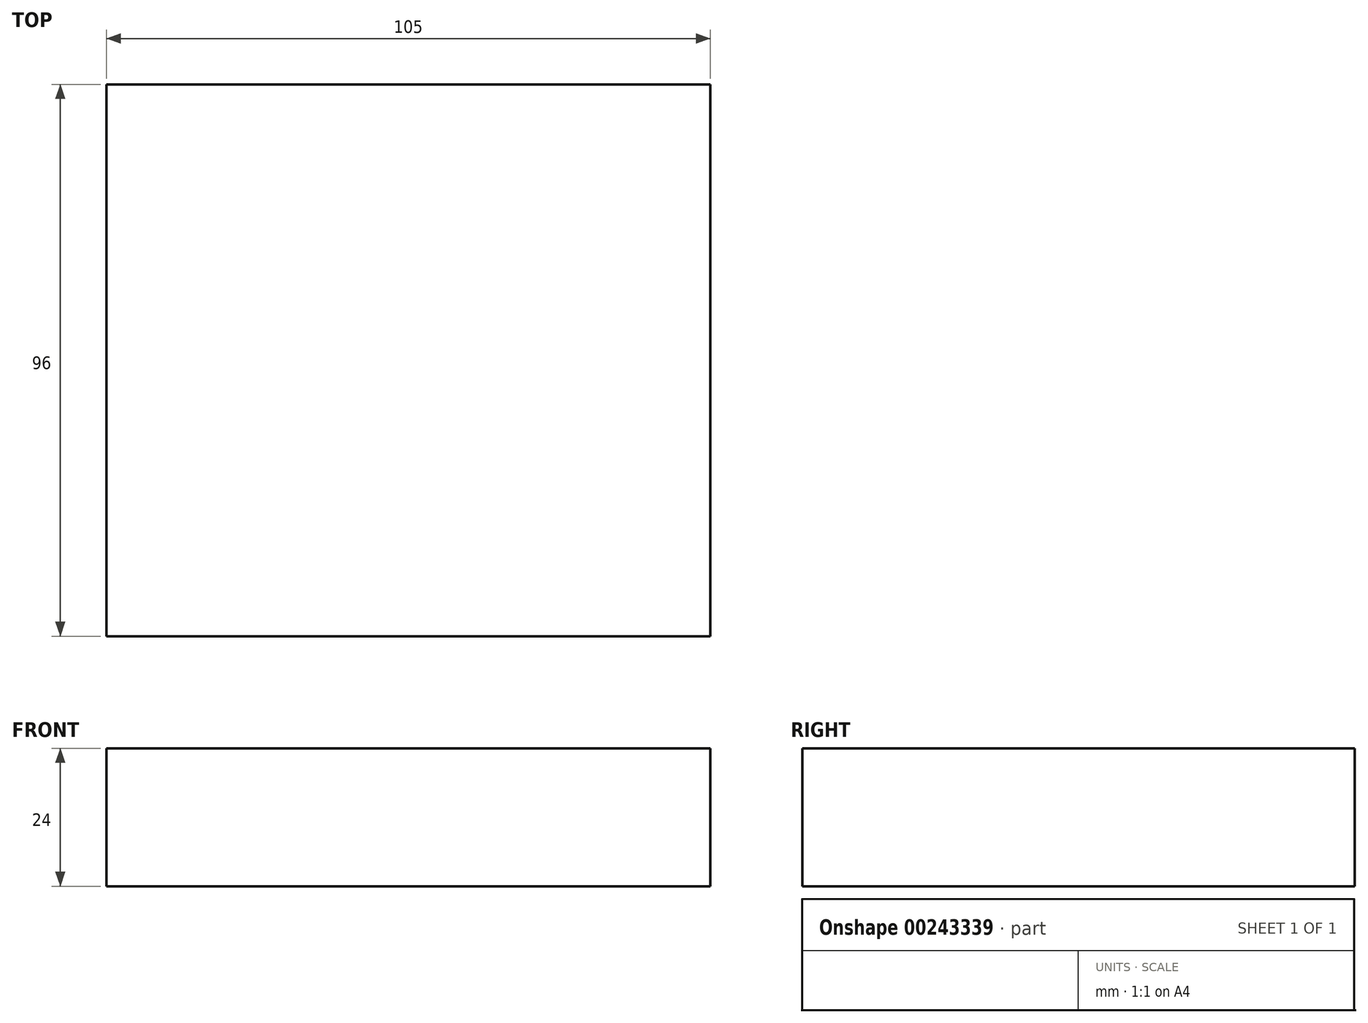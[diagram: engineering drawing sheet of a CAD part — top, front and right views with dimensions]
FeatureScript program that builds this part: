
annotation { "Feature Type Name" : "Feature", "Feature Type Description" : "" }
export const myFeature = defineFeature(function(context is Context, id is Id, definition is map)
    precondition{}
    {
        {
            var Q0;
            Q0=qCreatedBy(makeId("Top.planeOp"),FACE);
            var sketch = newSketch(context, id + "F0", { "sketchPlane" : qUnion([Q0])});
            skLineSegment(sketch, "E0.bottom", {"start": v(-52.5, 48) * mm, "end": v(52.5, 48) * mm});
            skLineSegment(sketch, "E0.top", {"start": v(-52.5, -48) * mm, "end": v(52.5, -48) * mm});
            skLineSegment(sketch, "E0.left", {"start": v(-52.5, 48) * mm, "end": v(-52.5, -48) * mm});
            skLineSegment(sketch, "E0.right", {"start": v(52.5, 48) * mm, "end": v(52.5, -48) * mm});
            skPoint(sketch, "E0.middle", {"position": v(0, 0) * mm});
            skSolve(sketch);
        }
        {
            var Q0;
            Q0 = qSketchRegion(id + "F0", true);
            extrude(context, id + "F1", {"entities" : qUnion([Q0]), "depth" : 24 * mm});
        }
    });
